FCSTD DOCUMENT  (FreeCAD 0.15R4641 (Git))
Label: pawn-v001
License: CC-BY 3.0
LicenseURL: http://creativecommons.org/licenses/by/3.0/
objects: Sketcher::SketchObject×1, PartDesign::Revolution×1
note: 3 computed .brp shape members not serialized (recipe doc carries the construction recipe); baked Part::Feature solids carry a one-line shape summary decoded from their .brp

FEATURE [Sketcher::SketchObject] Sketch
  Placement = pos=(0,0,0) rot=(-1,0,0;4.71239rad)
  sketch-geometry (9):
    g0: ArcOfCircle CenterX=-5 CenterY=4 CenterZ=0 NormalX=0 NormalY=0 NormalZ=1 Radius=4 StartAngle=1.5708 EndAngle=4.71239
    g1: ArcOfCircle CenterX=5 CenterY=4 CenterZ=0 NormalX=0 NormalY=0 NormalZ=1 Radius=4 StartAngle=4.71239 EndAngle=7.85398
    g2: LineSegment StartX=-5 StartY=0 StartZ=0 EndX=5 EndY=0 EndZ=0
    g3: LineSegment StartX=-5 StartY=8 StartZ=0 EndX=-3 EndY=8 EndZ=0
    g4: LineSegment StartX=3 StartY=0 StartZ=0 EndX=-3 EndY=0 EndZ=0
    g5: LineSegment StartX=3 StartY=8 StartZ=0 EndX=5 EndY=8 EndZ=0
    g6: LineSegment StartX=-3 StartY=21 StartZ=0 EndX=-3 EndY=8 EndZ=0
    g7: LineSegment StartX=3 StartY=21 StartZ=0 EndX=3 EndY=8 EndZ=0
    g8: ArcOfCircle CenterX=0 CenterY=25 CenterZ=0 NormalX=0 NormalY=0 NormalZ=1 Radius=5 StartAngle=5.35589 EndAngle=10.3521
  constraints (25):
    c: Tangent(g0,g3) = 1.5708
    c: Tangent(g0,g2) = -1.5708
    c: Tangent(g2,g1) = -1.5708
    c: Tangent(g5,g1) = 1.5708
    c: Horizontal(g2)
    c: Tangent(g1,g-1)
    c: Horizontal(g4)
    c: PointOnObject(g4,g2)
    c: DistanceX(g0,g1) = 10
    c: Radius(g1) = 4
    c: Symmetric(g0,g1,g-2)
    c: Tangent(g3,g5)
    c: Coincident(g6,g3)
    c: Vertical(g6)
    c: Coincident(g7,g5)
    c: Vertical(g7)
    c: DistanceX(g3,g5) = 6
    c: DistanceX(g-1,g3) = -3
    c: DistanceX(g5,g4) = 0
    c: DistanceX(g4,g3) = 0
    c: Coincident(g8,g6)
    c: Coincident(g8,g7)
    c: DistanceY(g-1,g8) = 25
    c: Radius(g8) = 5
    c: Equal(g7,g6)
FEATURE [PartDesign::Revolution] Revolution
  Angle = 360
  Axis = (1,0,0)
  Base = (0,0,0)
  Placement = pos=(0,0,0) rot=(-1,0,0;4.71239rad)
  ReferenceAxis = -> Sketch [H_Axis]
  Sketch = -> Sketch
